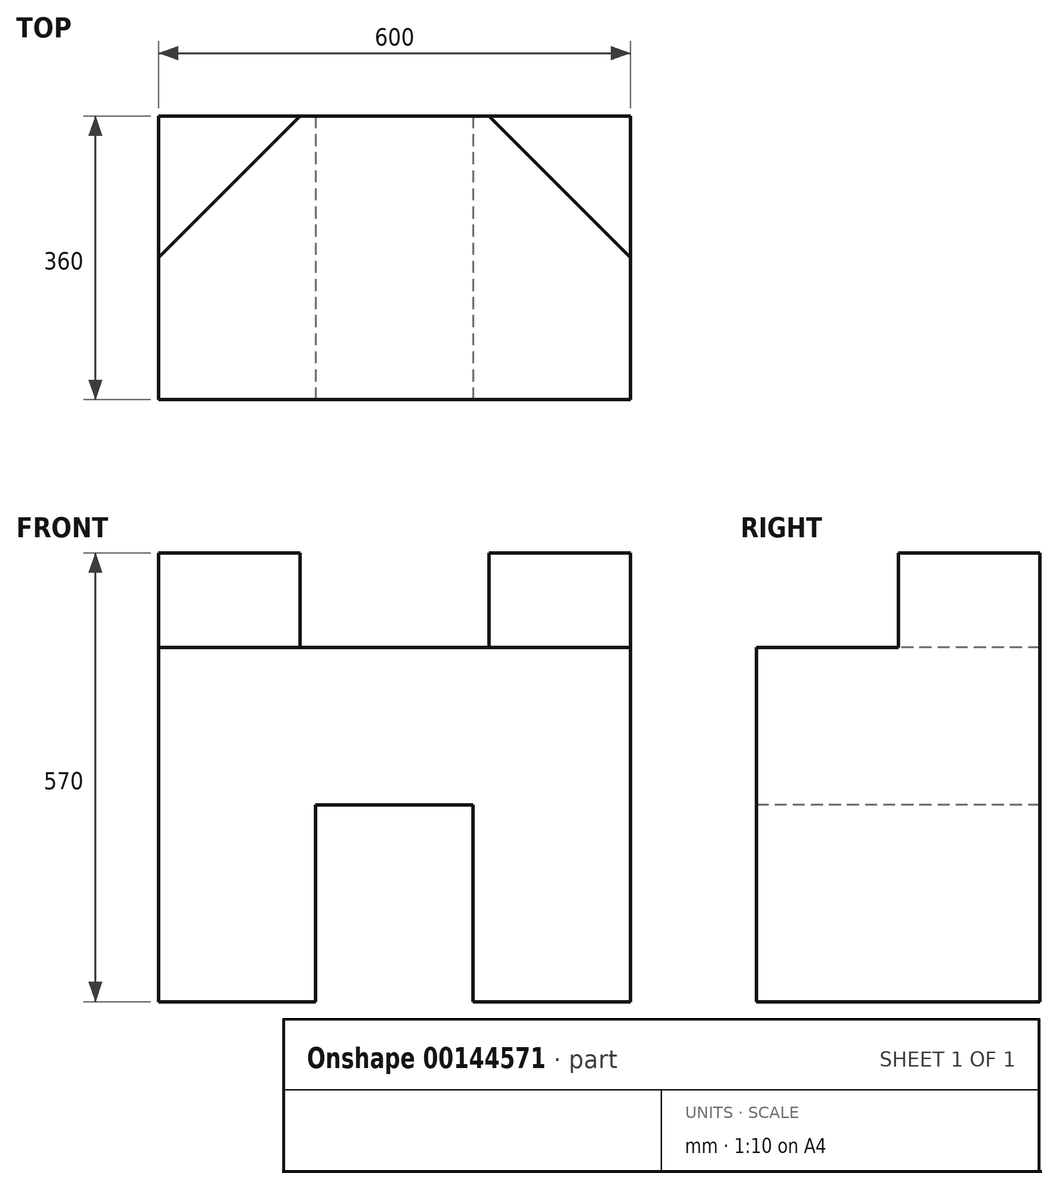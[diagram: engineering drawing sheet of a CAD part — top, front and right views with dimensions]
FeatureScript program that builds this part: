
annotation { "Feature Type Name" : "Feature", "Feature Type Description" : "" }
export const myFeature = defineFeature(function(context is Context, id is Id, definition is map)
    precondition{}
    {
        {
            var Q0;
            Q0=qCreatedBy(makeId("Front.planeOp"),FACE);
            var sketch = newSketch(context, id + "F0", { "sketchPlane" : qUnion([Q0])});
            skLineSegment(sketch, "E0.bottom", {"start": v(-300, -285) * mm, "end": v(300, -285) * mm});
            skLineSegment(sketch, "E0.top", {"start": v(-300, 285) * mm, "end": v(300, 285) * mm});
            skLineSegment(sketch, "E0.left", {"start": v(-300, -285) * mm, "end": v(-300, 285) * mm});
            skLineSegment(sketch, "E0.right", {"start": v(300, -285) * mm, "end": v(300, 285) * mm});
            skPoint(sketch, "E0.middle", {"position": v(0, 0) * mm});
            skSolve(sketch);
        }
        {
            var Q0;
            Q0 = qSketchRegion(id + "F0", true);
            extrude(context, id + "F1", {"entities" : qUnion([Q0]), "depth" : 360 * mm});
        }
        {
            var Q0;
            Q0=makeQuery(id+"F1.opExtrude","SWEPT_FACE",FACE,{"disambiguationData":[OSD([sQuery(id+"F0.wireOp",EDGE,"E0.top")])]});
            var sketch = newSketch(context, id + "F2", { "sketchPlane" : qUnion([Q0])});
            skLineSegment(sketch, "E1.bottom", {"start": v(-300, -360) * mm, "end": v(300, -360) * mm});
            skLineSegment(sketch, "E1.top", {"start": v(-300, -180) * mm, "end": v(300, -180) * mm});
            skLineSegment(sketch, "E1.left", {"start": v(-300, -360) * mm, "end": v(-300, -180) * mm});
            skLineSegment(sketch, "E1.right", {"start": v(300, -360) * mm, "end": v(300, -180) * mm});
            skLineSegment(sketch, "E2", {"start": v(-300, -180) * mm, "end": v(-120, 0) * mm});
            skLineSegment(sketch, "E3", {"start": v(-120, 0) * mm, "end": v(120, 0) * mm});
            skLineSegment(sketch, "E4", {"start": v(120, 0) * mm, "end": v(300, -180) * mm});
            skPoint(sketch, "E5", {"position": v(0, 0) * mm});
            skSolve(sketch);
        }
        {
            var Q0;
            Q0 = qSketchRegion(id + "F2", true);
            extrude(context, id + "F3", {"entities" : qUnion([Q0]), "operationType" : NewBodyOperationType.REMOVE, "oppositeDirection" : true, "depth" : 120 * mm});
        }
        {
            var Q0;
            Q0=makeQuery(id+"F1.opExtrude","CAP_FACE",FACE,{"disambiguationData":[OSD([sQuery(id+"F0.wireOp",EDGE,"E0.bottom"),sQuery(id+"F0.wireOp",EDGE,"E0.top"),sQuery(id+"F0.wireOp",EDGE,"E0.left"),sQuery(id+"F0.wireOp",EDGE,"E0.right")])],"isStart":false});
            var sketch = newSketch(context, id + "F4", { "sketchPlane" : qUnion([Q0])});
            skPoint(sketch, "E6", {"position": v(0, -285) * mm});
            skLineSegment(sketch, "E7.bottom", {"start": v(-100, -285) * mm, "end": v(100, -285) * mm});
            skLineSegment(sketch, "E7.top", {"start": v(-100, -35) * mm, "end": v(100, -35) * mm});
            skLineSegment(sketch, "E7.left", {"start": v(-100, -285) * mm, "end": v(-100, -35) * mm});
            skLineSegment(sketch, "E7.right", {"start": v(100, -285) * mm, "end": v(100, -35) * mm});
            skSolve(sketch);
        }
        {
            var Q0;
            Q0 = qSketchRegion(id + "F4", true);
            extrude(context, id + "F5", {"entities" : qUnion([Q0]), "operationType" : NewBodyOperationType.REMOVE, "endBound" : BoundingType.THROUGH_ALL, "oppositeDirection" : true, "depth" : 25 * mm});
        }
    });
